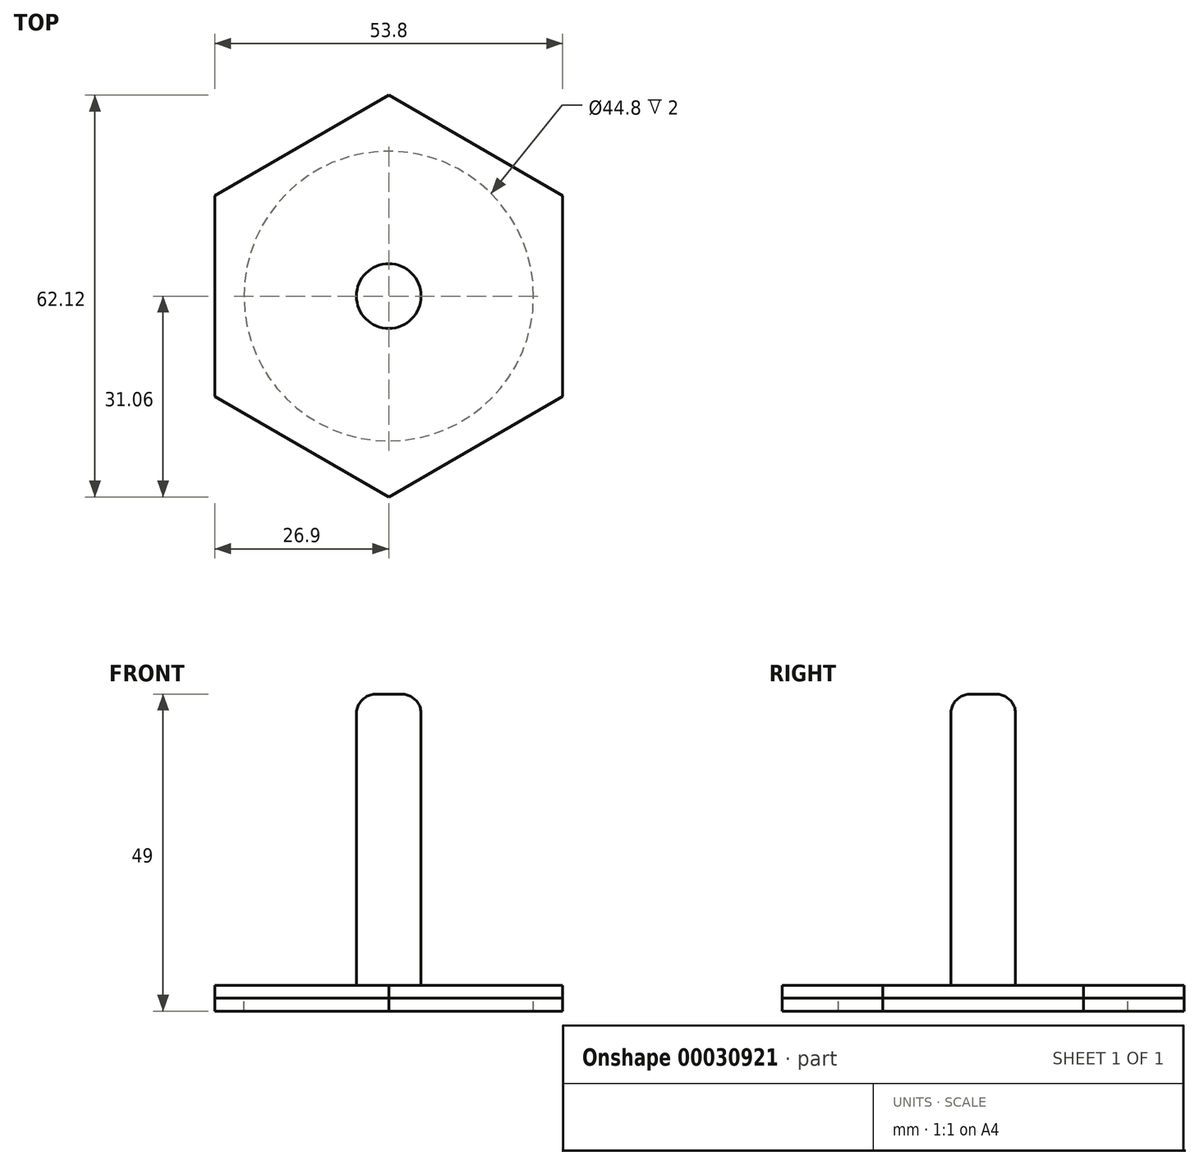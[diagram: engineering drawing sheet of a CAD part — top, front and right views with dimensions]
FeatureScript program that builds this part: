
annotation { "Feature Type Name" : "Feature", "Feature Type Description" : "" }
export const myFeature = defineFeature(function(context is Context, id is Id, definition is map)
    precondition{}
    {
        {
            var Q0;
            Q0=qCreatedBy(makeId("Top.planeOp"),FACE);
            var sketch = newSketch(context, id + "F0", { "sketchPlane" : qUnion([Q0])});
            skCircle(sketch, "E0.cCircle", {"center": v(0, 0) * mm, "radius": 26.9 * mm, "construction": true});
            skLineSegment(sketch, "E0.0", {"start": v(26.9, 15.53) * mm, "end": v(26.9, -15.53) * mm});
            skLineSegment(sketch, "E0.1", {"start": v(26.9, -15.53) * mm, "end": v(0, -31.06) * mm});
            skLineSegment(sketch, "E0.2", {"start": v(0, -31.06) * mm, "end": v(-26.9, -15.53) * mm});
            skLineSegment(sketch, "E0.3", {"start": v(-26.9, -15.53) * mm, "end": v(-26.9, 15.53) * mm});
            skLineSegment(sketch, "E0.4", {"start": v(-26.9, 15.53) * mm, "end": v(0, 31.06) * mm});
            skLineSegment(sketch, "E0.5", {"start": v(0, 31.06) * mm, "end": v(26.9, 15.53) * mm});
            skPoint(sketch, "E0.0.midPoint", {"position": v(26.9, 0) * mm});
            skCircle(sketch, "E1", {"center": v(0, 0) * mm, "radius": 22.4 * mm});
            skSolve(sketch);
        }
        {
            var Q0;
            Q0=makeQuery(id+"F0.imprint","IMPRINT",FACE,{"disambiguationData":[TD([[makeQuery(id+"F0.imprint","IMPRINT",EDGE,{"derivedFrom":sQuery(id+"F0.wireOp",EDGE,"E0.0")}),-1.0]])]});
            var Q1;
            Q1=makeQuery(id+"F0.imprint","IMPRINT",FACE,{"disambiguationData":[TD([[makeQuery(id+"F0.imprint","IMPRINT",EDGE,{"derivedFrom":sQuery(id+"F0.wireOp",EDGE,"E1")}),1.0]])]});
            extrude(context, id + "F1", {"entities" : qUnion([Q0, Q1]), "depth" : 2 * mm});
        }
        {
            var Q0;
            Q0=makeQuery(id+"F1.opExtrude","CAP_FACE",FACE,{"disambiguationData":[OSD([sQuery(id+"F0.wireOp",EDGE,"E0.0"),sQuery(id+"F0.wireOp",EDGE,"E0.1"),sQuery(id+"F0.wireOp",EDGE,"E0.2"),sQuery(id+"F0.wireOp",EDGE,"E0.3"),sQuery(id+"F0.wireOp",EDGE,"E0.4"),sQuery(id+"F0.wireOp",EDGE,"E0.5")])],"isStart":false});
            var sketch = newSketch(context, id + "F2", { "sketchPlane" : qUnion([Q0])});
            skCircle(sketch, "E2", {"center": v(0, 0) * mm, "radius": 5 * mm});
            skSolve(sketch);
        }
        {
            var Q0;
            Q0=makeQuery(id+"F2.imprint","IMPRINT",FACE,{"disambiguationData":[TD([[makeQuery(id+"F2.imprint","IMPRINT",EDGE,{"derivedFrom":sQuery(id+"F2.wireOp",EDGE,"E2")}),1.0]])]});
            var Q1;
            Q1=sQuery(id+"F075zKwJdN0EvCG_1.wireOp",EDGE,"236aaeca-1080-4ac4-92cc-dae40a2d3b87");
            extrude(context, id + "F3", {"entities" : qUnion([Q0]), "operationType" : NewBodyOperationType.ADD, "surfaceEntities" : qUnion([Q1]), "depth" : 45 * mm});
        }
        {
            var Q0;
            Q0=makeQuery(id+"F3.opExtrude","CAP_EDGE",EDGE,{"disambiguationData":[OSD([sQuery(id+"F075zKwJdN0EvCG_1.wireOp",EDGE,"236aaeca-1080-4ac4-92cc-dae40a2d3b87")])],"isStart":false});
            var Q1;
            Q1=makeQuery(id+"F3.opExtrude","CAP_EDGE",EDGE,{"disambiguationData":[OSD([sQuery(id+"F075zKwJdN0EvCG_1.wireOp",EDGE,"bd78913b-6ae2-4fef-a7e5-6946d027fed9.1.0")])],"isStart":false});
            var Q2;
            Q2=makeQuery(id+"F3.opExtrude","CAP_EDGE",EDGE,{"disambiguationData":[OSD([sQuery(id+"F075zKwJdN0EvCG_1.wireOp",EDGE,"bd78913b-6ae2-4fef-a7e5-6946d027fed9.2.0")])],"isStart":false});
            var Q3;
            Q3=makeQuery(id+"F3.opExtrude","CAP_EDGE",EDGE,{"disambiguationData":[OSD([sQuery(id+"F2.wireOp",EDGE,"E2")])],"isStart":false});
            fillet(context, id + "F4", {"entities" : qUnion([Q0, Q1, Q2, Q3]), "radius" : 3 * mm, "tangentPropagation" : true, "allowEdgeOverflow" : false});
        }
        {
            var Q0;
            Q0=makeQuery(id+"F0.imprint","IMPRINT",FACE,{"disambiguationData":[TD([[makeQuery(id+"F0.imprint","IMPRINT",EDGE,{"derivedFrom":sQuery(id+"F0.wireOp",EDGE,"E1")}),1.0]])]});
            extrude(context, id + "F5", {"entities" : qUnion([Q0]), "operationType" : NewBodyOperationType.ADD, "oppositeDirection" : true, "depth" : 2 * mm});
        }
        {
            var Q0;
            Q0=makeQuery(id+"F0.imprint","IMPRINT",FACE,{"disambiguationData":[TD([[makeQuery(id+"F0.imprint","IMPRINT",EDGE,{"derivedFrom":sQuery(id+"F0.wireOp",EDGE,"E0.0")}),-1.0]])]});
            extrude(context, id + "F6", {"entities" : qUnion([Q0]), "oppositeDirection" : true, "depth" : 2 * mm});
        }
    });
